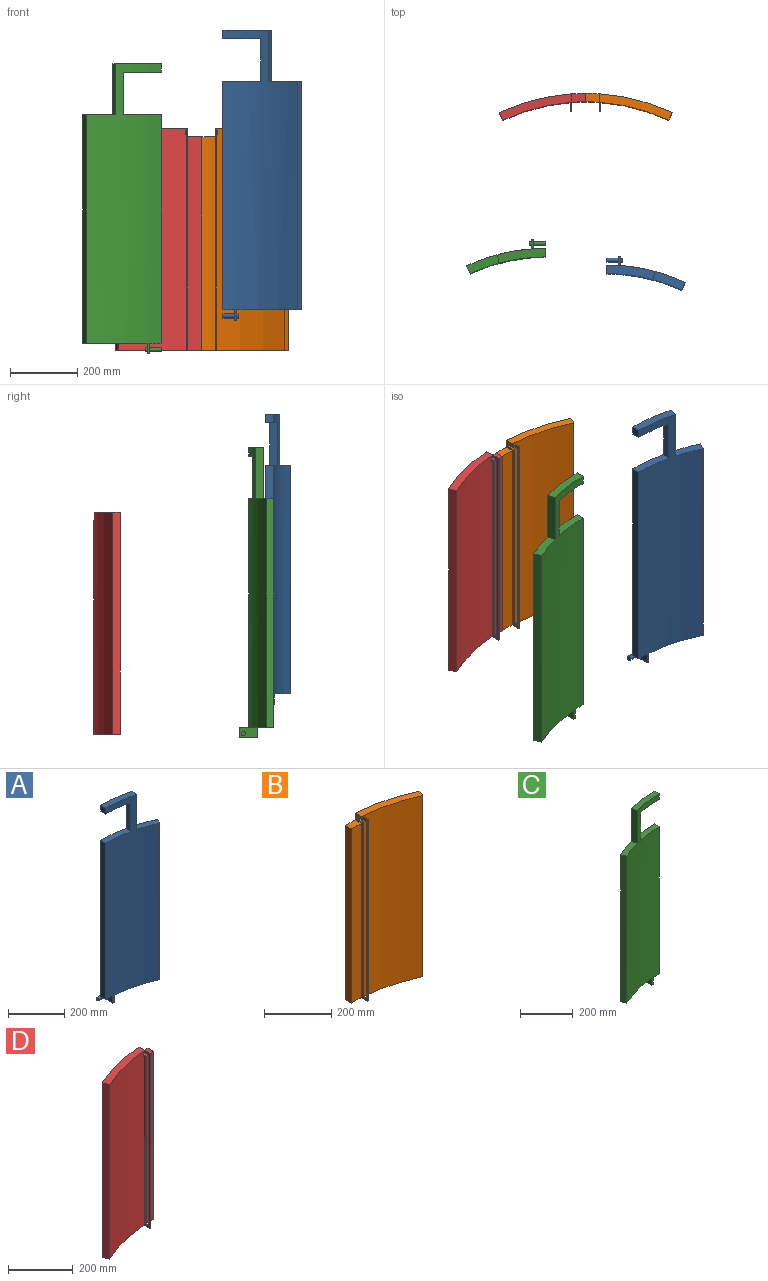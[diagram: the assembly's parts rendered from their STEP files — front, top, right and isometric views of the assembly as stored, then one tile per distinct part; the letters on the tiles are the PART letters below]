
ASSEMBLY  parts=4 mates=1
PART A: 22 faces, bbox 233.5x101.9x863.6 mm
  f0: plane 679.45x25.4mm, normal (-1,0,0), area 17258mm2, adj f5,f8,f11,f20
  f1: plane 97.07x55.96mm, normal (0,0,1), area 2392.8mm2, adj f5,f10,f11,f17
  f2: plane 54.13x31.75mm, normal (1,0,0), area 1591.8mm2, adj f3,f5,f6,f7,f12,f15
  f3: plane 31.75x6.35mm, normal (0,1,0), area 201.6mm2, adj f2,f4,f6,f7
  f4: plane 53.67x31.75mm, normal (-1,0,0), area 1577.2mm2, adj f3,f5,f6,f7,f8,f14
  f5: cylinder r=527.05mm len=863.6mm, axis (0,0,-1), area 163186.3mm2, adj f0,f1,f2,f4,f7,f8,f9,f10
  f6: plane 28.65x6.35mm, normal (0,0,1), area 180.5mm2, adj f2,f3,f4,f11
  f7: plane 54.13x6.35mm, normal (0,0,-1), area 342.2mm2, adj f2,f3,f4,f5
  f8: plane 34.93x26.56mm, normal (0,0,-1), area 887.7mm2, adj f0,f4,f5,f11
  f9: plane 25.4x25.4mm, normal (-1,0,0), area 645.2mm2, adj f5,f11,f18,f21
  f10: plane 679.45x23.02mm, normal (0.91,-0.42,0), area 17258mm2, adj f1,f5,f11,f12
  f11: cylinder r=552.45mm len=831.85mm, axis (0,0,-1), area 170683.2mm2, adj f0,f1,f6,f8,f9,f10,f12,f17
  f12: plane 192.2x73.24mm, normal (0,0,-1), area 4932.6mm2, adj f2,f5,f10,f11
  f13: plane 12.7x12.7mm, normal (-1,0,0), area 126.7mm2, adj f14
  f14: cylinder r=6.35mm len=34.93mm, axis (1,0,0), area 1393.4mm2, adj f4,f13
  f15: cylinder r=6.35mm len=12.7mm, axis (1,0,0), area 253.4mm2, adj f2,f16
  f16: plane 12.7x12.7mm, normal (1,0,0), area 126.7mm2, adj f15
  f17: plane 152.4x24.53mm, normal (0.97,-0.26,0), area 3871mm2, adj f1,f5,f11,f18
  f18: plane 142.98x43.36mm, normal (0,0,1), area 3589.2mm2, adj f5,f9,f11,f17
  f19: plane 127x24.56mm, normal (-0.97,0.26,0), area 3229.4mm2, adj f5,f11,f20,f21
  f20: plane 118.3x37.38mm, normal (0,0,1), area 2943.8mm2, adj f0,f5,f11,f19
  f21: plane 118.3x37.38mm, normal (0,0,-1), area 2943.8mm2, adj f5,f9,f11,f19
PART B: 21 faces, bbox 257.5x79.8x660.4 mm
  f0: plane 660.4x52.03mm, normal (-1,0,0), area 10026.8mm2, adj f4,f5,f7,f8,f10,f11,f12,f13
  f1: plane 660.4x26.88mm, normal (1,0,0), area 9457.2mm2, adj f2,f5,f7,f8,f12,f13,f14,f15
  f2: cylinder r=584.2mm len=660.4mm, axis (0,0,-1), area 138915.9mm2, adj f1,f6,f7,f8,f17,f18,f19
  f3: cylinder r=609.28mm len=660.4mm, axis (0,0,-1), area 174437.3mm2, adj f4,f6,f7,f8,f9,f11
  f4: plane 25.4x3.18mm, normal (0,1,0), area 80.6mm2, adj f0,f3,f7,f11
  f5: plane 660.4x3.18mm, normal (0,-1,0), area 2096.8mm2, adj f0,f1,f7,f8
  f6: plane 660.4x22.73mm, normal (0.91,-0.42,0), area 16565mm2, adj f2,f3,f7,f8
  f7: plane 216.22x78.19mm, normal (0,0,1), area 5580.4mm2, adj f0,f1,f2,f3,f4,f5,f6
  f8: plane 257.49x79.82mm, normal (0,0,-1), area 6616.9mm2, adj f0,f1,f2,f3,f5,f6,f9,f10
  f9: plane 635x25.08mm, normal (-1,0,0), area 15927.9mm2, adj f3,f8,f10,f11
  f10: cylinder r=584.2mm len=635mm, axis (0,0,-1), area 26231.5mm2, adj f0,f8,f9,f11
  f11: plane 44.45x26.54mm, normal (0,0,1), area 1036.5mm2, adj f0,f3,f4,f9,f10
  f12: plane 3.18x0.16mm, normal (0,0.7,0.72), area 0.7mm2, adj f0,f1,f13,f17
  f13: plane 628.8x3.18mm, normal (0,-1,0), area 1996.5mm2, adj f0,f1,f12,f14
  f14: cylinder r=6.35mm len=12.7mm, axis (-1,0,0), area 63.3mm2, adj f0,f1,f13,f15
  f15: plane 635x3.18mm, normal (0,1,0), area 2016.1mm2, adj f0,f1,f14,f16
  f16: cylinder r=6.35mm len=6.35mm, axis (-1,0,0), area 31.7mm2, adj f0,f1,f15,f18
  f17: plane 19.51x6.35mm, normal (0,0,1), area 100.9mm2, adj f0,f1,f2,f12,f19,f20
  f18: plane 26.01x6.35mm, normal (0,0,-1), area 121.5mm2, adj f0,f1,f2,f16,f19,f20
  f19: plane 18.75x12.7mm, normal (-1,0,0), area 220.8mm2, adj f2,f17,f18,f20
  f20: cylinder r=6.35mm len=12.7mm, axis (-1,0,0), area 126.7mm2, adj f0,f17,f18,f19
PART C: 22 faces, bbox 233.5x101.9x863.6 mm
  f0: plane 679.45x25.4mm, normal (1,0,0), area 17258mm2, adj f5,f8,f11,f20
  f1: plane 97.07x55.96mm, normal (0,0,1), area 2392.8mm2, adj f5,f10,f11,f17
  f2: plane 54.13x31.75mm, normal (-1,0,0), area 1591.8mm2, adj f3,f5,f6,f7,f12,f15
  f3: plane 31.75x6.35mm, normal (0,1,0), area 201.6mm2, adj f2,f4,f6,f7
  f4: plane 53.67x31.75mm, normal (1,0,0), area 1577.2mm2, adj f3,f5,f6,f7,f8,f14
  f5: cylinder r=527.05mm len=863.6mm, axis (0,0,-1), area 163186.3mm2, adj f0,f1,f2,f4,f7,f8,f9,f10
  f6: plane 28.65x6.35mm, normal (0,0,1), area 180.5mm2, adj f2,f3,f4,f11
  f7: plane 54.13x6.35mm, normal (0,0,-1), area 342.2mm2, adj f2,f3,f4,f5
  f8: plane 34.93x26.56mm, normal (0,0,-1), area 887.7mm2, adj f0,f4,f5,f11
  f9: plane 25.4x25.4mm, normal (1,0,0), area 645.2mm2, adj f5,f11,f18,f21
  f10: plane 679.45x23.02mm, normal (-0.91,-0.42,0), area 17258mm2, adj f1,f5,f11,f12
  f11: cylinder r=552.45mm len=831.85mm, axis (0,0,-1), area 170683.2mm2, adj f0,f1,f6,f8,f9,f10,f12,f17
  f12: plane 192.2x73.24mm, normal (0,0,-1), area 4932.6mm2, adj f2,f5,f10,f11
  f13: plane 12.7x12.7mm, normal (1,0,0), area 126.7mm2, adj f14
  f14: cylinder r=6.35mm len=34.93mm, axis (-1,0,0), area 1393.4mm2, adj f4,f13
  f15: cylinder r=6.35mm len=12.7mm, axis (-1,0,0), area 253.4mm2, adj f2,f16
  f16: plane 12.7x12.7mm, normal (-1,0,0), area 126.7mm2, adj f15
  f17: plane 152.4x24.53mm, normal (-0.97,-0.26,0), area 3871mm2, adj f1,f5,f11,f18
  f18: plane 142.98x43.36mm, normal (0,0,1), area 3589.2mm2, adj f5,f9,f11,f17
  f19: plane 127x24.56mm, normal (0.97,0.26,0), area 3229.4mm2, adj f5,f11,f20,f21
  f20: plane 118.3x37.38mm, normal (0,0,1), area 2943.8mm2, adj f0,f5,f11,f19
  f21: plane 118.3x37.38mm, normal (0,0,-1), area 2943.8mm2, adj f5,f9,f11,f19
PART D: 21 faces, bbox 257.5x79.8x660.4 mm
  f0: plane 660.4x52.03mm, normal (1,0,0), area 10026.8mm2, adj f4,f5,f7,f8,f10,f11,f12,f13
  f1: plane 660.4x26.88mm, normal (-1,0,0), area 9457.2mm2, adj f2,f5,f7,f8,f12,f13,f14,f15
  f2: cylinder r=584.2mm len=660.4mm, axis (0,0,-1), area 138915.9mm2, adj f1,f6,f7,f8,f17,f18,f19
  f3: cylinder r=609.28mm len=660.4mm, axis (0,0,-1), area 174437.3mm2, adj f4,f6,f7,f8,f9,f11
  f4: plane 25.4x3.18mm, normal (0,1,0), area 80.6mm2, adj f0,f3,f7,f11
  f5: plane 660.4x3.18mm, normal (0,-1,0), area 2096.8mm2, adj f0,f1,f7,f8
  f6: plane 660.4x22.73mm, normal (-0.91,-0.42,0), area 16565mm2, adj f2,f3,f7,f8
  f7: plane 216.22x78.19mm, normal (0,0,1), area 5580.4mm2, adj f0,f1,f2,f3,f4,f5,f6
  f8: plane 257.49x79.82mm, normal (0,0,-1), area 6616.9mm2, adj f0,f1,f2,f3,f5,f6,f9,f10
  f9: plane 635x25.08mm, normal (1,0,0), area 15927.9mm2, adj f3,f8,f10,f11
  f10: cylinder r=584.2mm len=635mm, axis (0,0,-1), area 26231.5mm2, adj f0,f8,f9,f11
  f11: plane 44.45x26.54mm, normal (0,0,1), area 1036.5mm2, adj f0,f3,f4,f9,f10
  f12: plane 3.18x0.16mm, normal (0,0.7,0.72), area 0.7mm2, adj f0,f1,f13,f17
  f13: plane 628.8x3.18mm, normal (0,-1,0), area 1996.5mm2, adj f0,f1,f12,f14
  f14: cylinder r=6.35mm len=12.7mm, axis (1,0,0), area 63.3mm2, adj f0,f1,f13,f15
  f15: plane 635x3.18mm, normal (0,1,0), area 2016.1mm2, adj f0,f1,f14,f16
  f16: cylinder r=6.35mm len=6.35mm, axis (1,0,0), area 31.7mm2, adj f0,f1,f15,f18
  f17: plane 19.51x6.35mm, normal (0,0,1), area 100.9mm2, adj f0,f1,f2,f12,f19,f20
  f18: plane 26.01x6.35mm, normal (0,0,-1), area 121.5mm2, adj f0,f1,f2,f16,f19,f20
  f19: plane 18.75x12.7mm, normal (1,0,0), area 220.8mm2, adj f2,f17,f18,f20
  f20: cylinder r=6.35mm len=12.7mm, axis (1,0,0), area 126.7mm2, adj f0,f17,f18,f19
PLACE A t=(184.25,-49.56,99.7)mm
PLACE B t=(121.1,404.83,10.76)mm
PLACE C at identity
PLACE D t=(121.1,404.83,10.76)mm
MATE fastened D.f9 <-> B.f9  axis (1,0,0) through (121.1,1001.57,645.76)mm
